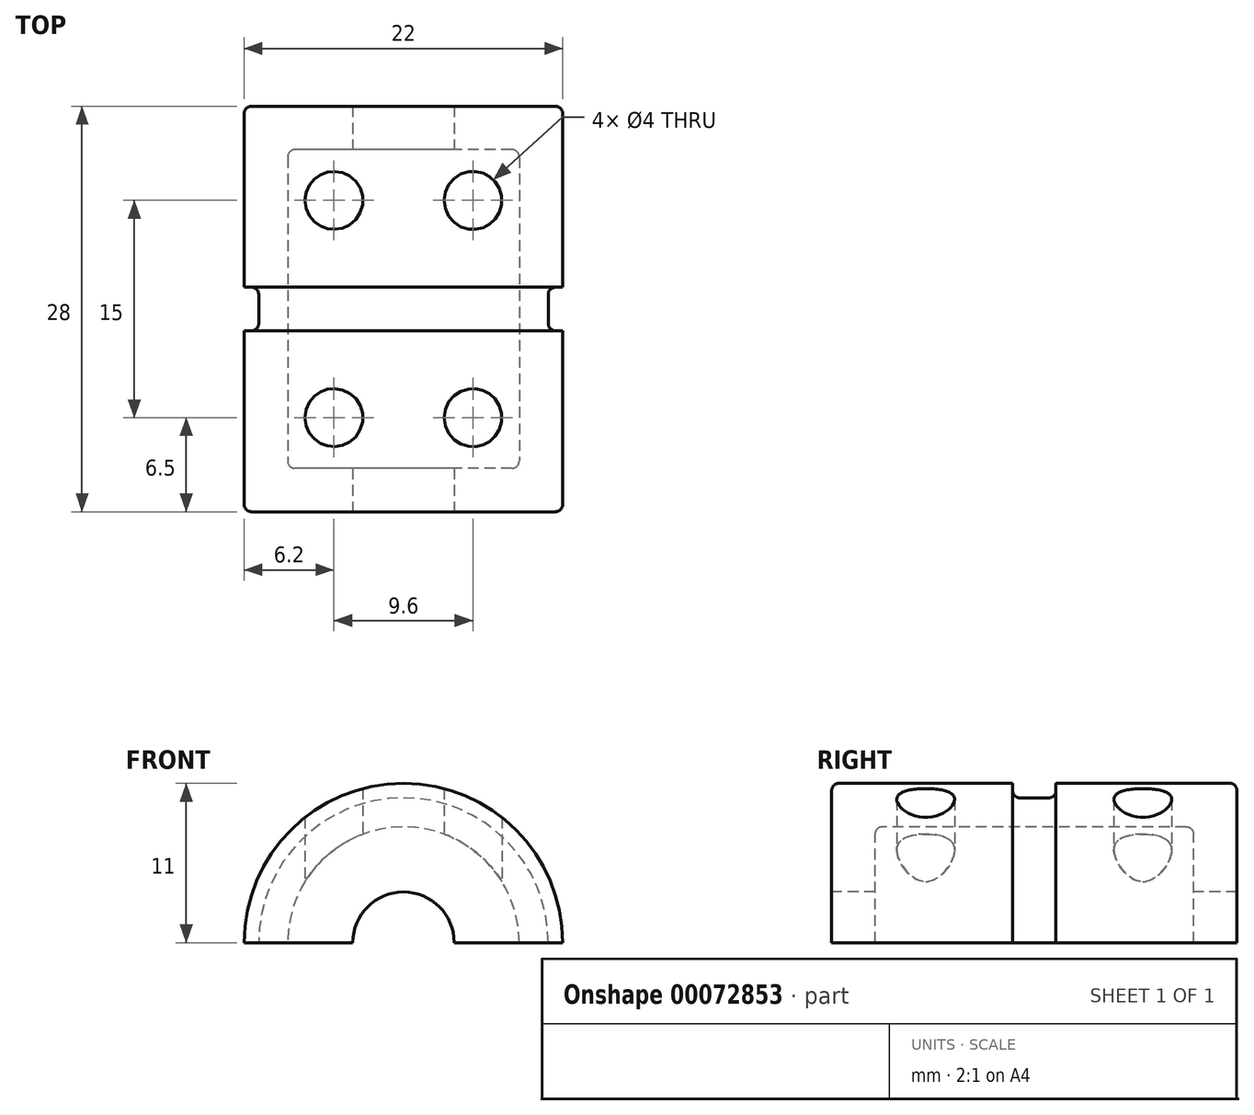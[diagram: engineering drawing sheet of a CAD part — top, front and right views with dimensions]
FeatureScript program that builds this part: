
annotation { "Feature Type Name" : "Feature", "Feature Type Description" : "" }
export const myFeature = defineFeature(function(context is Context, id is Id, definition is map)
    precondition{}
    {
        {
            var Q0;
            Q0=qCreatedBy(makeId("Front.planeOp"),FACE);
            var sketch = newSketch(context, id + "F0", { "sketchPlane" : qUnion([Q0])});
            skArc(sketch, "E0", {"start": v(11, 0) * mm, "mid": v(0, 11) * mm, "end": v(-11, 0) * mm});
            skLineSegment(sketch, "E1", {"start": v(-11, 0) * mm, "end": v(-8, 0) * mm});
            skLineSegment(sketch, "E2", {"start": v(11, 0) * mm, "end": v(8, 0) * mm});
            skArc(sketch, "E3", {"start": v(8, 0) * mm, "mid": v(0, 8) * mm, "end": v(-8, 0) * mm, "construction": true});
            skLineSegment(sketch, "E4", {"start": v(-8, 0) * mm, "end": v(8, 0) * mm});
            skSolve(sketch);
        }
        {
            var Q0;
            Q0 = qSketchRegion(id + "F0", true);
            var Q1;
            Q1 = qConstructionFilter(qBodyType(qCreatedBy(id + "F0" ,EDGE), BodyType.WIRE), ConstructionObject.NO);
            extrude(context, id + "F1", {"entities" : qUnion([Q0]), "surfaceEntities" : qUnion([Q1]), "endBound" : BoundingType.SYMMETRIC, "depth" : 28 * mm});
        }
        {
            var Q0;
            Q0=qCreatedBy(makeId("Front.planeOp"),FACE);
            var sketch = newSketch(context, id + "F2", { "sketchPlane" : qUnion([Q0])});
            skCircle(sketch, "E5", {"center": v(0, 0) * mm, "radius": 8 * mm});
            skSolve(sketch);
        }
        {
            var Q0;
            Q0 = qSketchRegion(id + "F2", true);
            extrude(context, id + "F3", {"entities" : qUnion([Q0]), "operationType" : NewBodyOperationType.REMOVE, "endBound" : BoundingType.SYMMETRIC, "oppositeDirection" : true, "depth" : (22) * mm});
        }
        {
            var Q0;
            Q0=qCreatedBy(makeId("Front.planeOp"),FACE);
            var sketch = newSketch(context, id + "F4", { "sketchPlane" : qUnion([Q0])});
            skCircle(sketch, "E6", {"center": v(0, 0) * mm, "radius": 3.5 * mm});
            skSolve(sketch);
        }
        {
            var Q0;
            Q0 = qSketchRegion(id + "F4", true);
            extrude(context, id + "F5", {"entities" : qUnion([Q0]), "operationType" : NewBodyOperationType.REMOVE, "endBound" : BoundingType.THROUGH_ALL, "oppositeDirection" : true, "depth" : 25 * mm, "hasSecondDirection" : true, "secondDirectionBound" : SecondDirectionBoundingType.THROUGH_ALL, "secondDirectionOppositeDirection" : false, "secondDirectionDepth" : 25 * mm});
        }
        {
            var Q0;
            Q0=qCreatedBy(makeId("Top.planeOp"),FACE);
            var sketch = newSketch(context, id + "F6", { "sketchPlane" : qUnion([Q0])});
            skCircle(sketch, "E7", {"center": v(4.8, 7.5) * mm, "radius": 2 * mm});
            skCircle(sketch, "E8.MirrorC", {"center": v(-4.8, 7.5) * mm, "radius": 2 * mm});
            skCircle(sketch, "E9.MirrorC", {"center": v(4.8, -7.5) * mm, "radius": 2 * mm});
            skCircle(sketch, "E10.MirrorC", {"center": v(-4.8, -7.5) * mm, "radius": 2 * mm});
            skSolve(sketch);
        }
        {
            var Q0;
            Q0 = qSketchRegion(id + "F6", true);
            extrude(context, id + "F7", {"entities" : qUnion([Q0]), "operationType" : NewBodyOperationType.REMOVE, "endBound" : BoundingType.THROUGH_ALL, "depth" : 25 * mm});
        }
        {
            var Q0;
            Q0=qCreatedBy(makeId("Front.planeOp"),FACE);
            var sketch = newSketch(context, id + "F8", { "sketchPlane" : qUnion([Q0])});
            skCircle(sketch, "E11", {"center": v(0, 0) * mm, "radius": 10 * mm});
            skCircle(sketch, "E12", {"center": v(0, 0) * mm, "radius": 11 * mm});
            skSolve(sketch);
        }
        {
            var Q0;
            Q0 = qSketchRegion(id + "F8", true);
            extrude(context, id + "F9", {"entities" : qUnion([Q0]), "operationType" : NewBodyOperationType.REMOVE, "endBound" : BoundingType.SYMMETRIC, "oppositeDirection" : true, "depth" : 3 * mm});
        }
        {
            var Q0;
            Q0=makeQuery(id+"F9.boolean.opBoolean","COPY",EDGE,{"derivedFrom":makeQuery(id+"F9.opExtrude","CAP_EDGE",EDGE,{"disambiguationData":[OSD([sQuery(id+"F8.wireOp",EDGE,"E11")])],"isStart":false})});
            var Q1;
            Q1=makeQuery(id+"F9.boolean.opBoolean","COPY",EDGE,{"derivedFrom":makeQuery(id+"F9.opExtrude","CAP_EDGE",EDGE,{"disambiguationData":[OSD([sQuery(id+"F8.wireOp",EDGE,"E11")])],"isStart":true})});
            var Q2;
            Q2=makeQuery(id+"F1.opExtrude","CAP_EDGE",EDGE,{"disambiguationData":[OSD([sQuery(id+"F0.wireOp",EDGE,"E0")])],"isStart":true});
            var Q3;
            Q3=makeQuery(id+"F1.opExtrude","CAP_EDGE",EDGE,{"disambiguationData":[OSD([sQuery(id+"F0.wireOp",EDGE,"E0")])],"isStart":false});
            var Q4;
            Q4=makeQuery(id+"F3.boolean.opBoolean","COPY",EDGE,{"derivedFrom":makeQuery(id+"F3.opExtrude","CAP_EDGE",EDGE,{"disambiguationData":[OSD([sQuery(id+"F2.wireOp",EDGE,"E5")])],"isStart":false})});
            var Q5;
            Q5=makeQuery(id+"F3.boolean.opBoolean","COPY",EDGE,{"derivedFrom":makeQuery(id+"F3.opExtrude","CAP_EDGE",EDGE,{"disambiguationData":[OSD([sQuery(id+"F2.wireOp",EDGE,"E5")])],"isStart":true})});
            fillet(context, id + "F10", {"entities" : qUnion([Q0, Q1, Q2, Q3, Q4, Q5]), "radius" : .5 * mm, "tangentPropagation" : true, "allowEdgeOverflow" : false});
        }
    });
